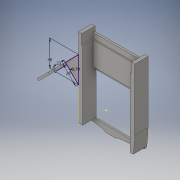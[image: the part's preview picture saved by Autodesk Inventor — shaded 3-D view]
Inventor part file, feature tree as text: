
AUTODESK INVENTOR PART (.ipt)
format: ipt  version: 2019 (Build 230136000, 136)  size: 239,104 bytes
history: mixed  units: in
note: dims shown in document units (in); Inventor stores cm internally (conversion verified against a paired STEP export)
features: extrude x10, sketch x7, projected_geometry x4, other x1, imported_body x1
ambient origin geometry x8: Origin, YZ Plane, XZ Plane, XY Plane, X Axis, Y Axis, Z Axis, Center Point
bodies: Solid1 (imported_parasolid)
feature tree (23):
  other  "base plate (1)"
  extrude  "Wyciągnięcie proste1"  Depth=0.3937in TaperAngle=0.0deg
  sketch  "Szkic3"
  extrude  "Wyciągnięcie proste2"  Depth=1.5748in
  extrude  "Wyciągnięcie proste3"  Depth=0.3937in TaperAngle=0.0deg
  extrude  "Wyciągnięcie proste4"  Depth=1.1024in
  extrude  "Wyciągnięcie proste5"  Depth=0.3092in
  sketch  "Szkic5"
  extrude  "Wyciągnięcie proste6"  Depth=0.9055in
  extrude  "Wyciągnięcie proste7"  Depth=0.1181in
  extrude  "Wyciągnięcie proste8"  Depth=0.3937in TaperAngle=0.0deg
  extrude  "Wyciągnięcie proste9"  Depth=1.0433in TaperAngle=0.0deg
  extrude  "Wyciągnięcie proste10"  Depth=0.1181in TaperAngle=0.0deg
  sketch  "Szkic2"
  sketch  "Szkic4"
  projected_geometry  "Pętla rzutowana1"
  projected_geometry  "Pętla rzutowana2"
  sketch  "Szkic6"
  projected_geometry  "Pętla rzutowana3"
  sketch  "Szkic7"
  sketch  "Szkic8"
  projected_geometry  "Pętla rzutowana4"
  imported_body  NMx_Import_Brep_tag  [imported B-rep: ~15 faces, bbox_mm=[72.4, 40.0, 4.5]]
